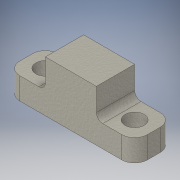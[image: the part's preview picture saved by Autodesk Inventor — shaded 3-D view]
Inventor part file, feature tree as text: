
AUTODESK INVENTOR PART (.ipt)
format: ipt  version: 2018 (Build 220112000, 112)  size: 143,360 bytes
history: native  units: in
note: dims shown in document units (in); Inventor stores cm internally (conversion verified against a paired STEP export)
features: sketch x3, extrude x2, fillet x2, mirror x1
ambient origin geometry x8: Origin, YZ Plane, XZ Plane, XY Plane, X Axis, Y Axis, Z Axis, Center Point
bodies: Solid1 (feature_tree)
feature tree (8):
  sketch  "Sketch1"  dims[d1=1.0in d3=0.75in d4=0.0in d5=0.25in d6=0.125in]
  extrude  "Extrusion1"  Depth=0.75in TaperAngle=0.0deg
  fillet  "Fillet1"  Radius=0.25in
  fillet  "Fillet2"  Radius=0.125in
  extrude  "Extrusion2"  Depth=0.375in
  mirror  "Mirror1"
  sketch  "Sketch2"  dims[d7=0.375in d8=0.375in]
  sketch  "Sketch3"  dims[d9=0.375in d10=0.75in d11=0.0in]
